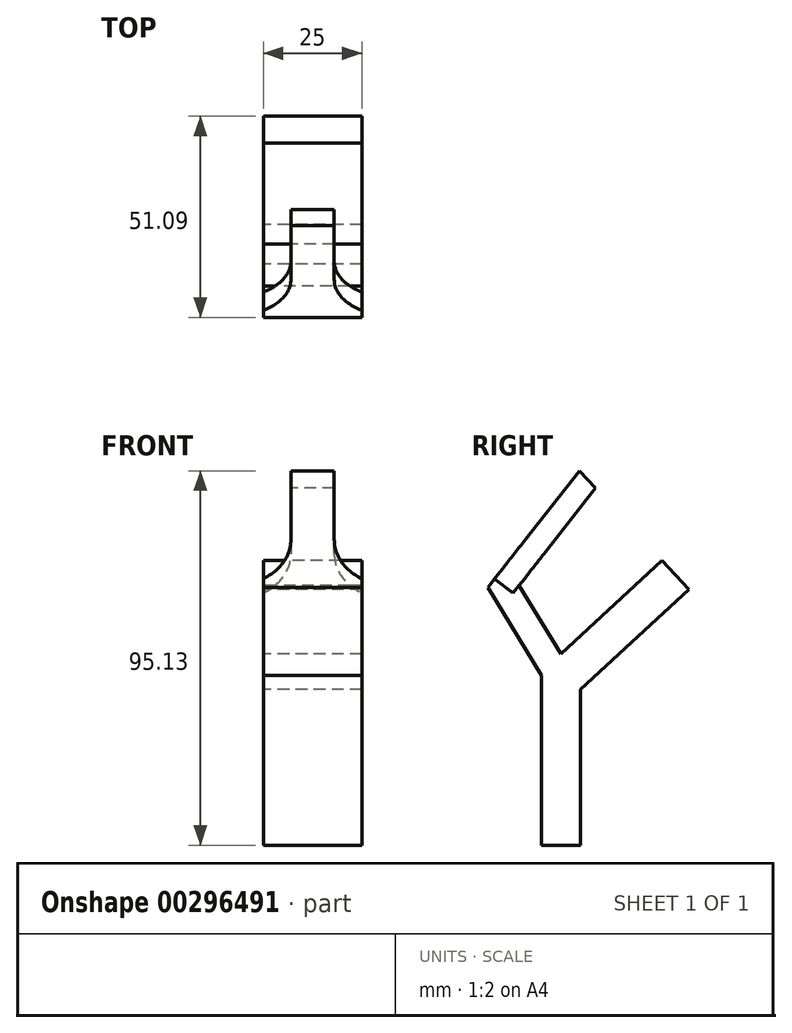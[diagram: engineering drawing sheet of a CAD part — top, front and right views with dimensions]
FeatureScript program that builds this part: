
annotation { "Feature Type Name" : "Feature", "Feature Type Description" : "" }
export const myFeature = defineFeature(function(context is Context, id is Id, definition is map)
    precondition{}
    {
        {
            var Q0;
            Q0=qCreatedBy(makeId("Right.planeOp"),FACE);
            var sketch = newSketch(context, id + "F0", { "sketchPlane" : qUnion([Q0])});
            skLineSegment(sketch, "E0", {"start": v(23.6, 39.62) * mm, "end": v(51.1, 65) * mm});
            skLineSegment(sketch, "E1", {"start": v(51.1, 65) * mm, "end": v(44.31, 72.35) * mm});
            skLineSegment(sketch, "E2", {"start": v(44.31, 72.35) * mm, "end": v(18.6, 48.6) * mm});
            skLineSegment(sketch, "E3", {"start": v(18.6, 48.6) * mm, "end": v(7.97, 66.02) * mm});
            skLineSegment(sketch, "E4", {"start": v(7.97, 66.02) * mm, "end": v(27.35, 90.72) * mm});
            skLineSegment(sketch, "E5", {"start": v(27.35, 90.72) * mm, "end": v(23.29, 95.13) * mm});
            skLineSegment(sketch, "E6", {"start": v(23.29, 95.13) * mm, "end": v(0, 65.46) * mm});
            skLineSegment(sketch, "E7", {"start": v(-34.13, 0) * mm, "end": v(0, 0) * mm});
            skLineSegment(sketch, "E8", {"start": v(51.1, 65) * mm, "end": v(27.45, 90.62) * mm, "construction": true});
            skLineSegment(sketch, "E9", {"start": v(18.6, 35) * mm, "end": v(18.6, 0) * mm, "construction": true});
            skLineSegment(sketch, "E10", {"start": v(13.6, 43.2) * mm, "end": v(13.6, 0) * mm});
            skLineSegment(sketch, "E11", {"start": v(13.6, 0) * mm, "end": v(23.6, 0) * mm});
            skLineSegment(sketch, "E12", {"start": v(23.6, 0) * mm, "end": v(23.6, 39.62) * mm});
            skLineSegment(sketch, "E13", {"start": v(0, 65.46) * mm, "end": v(13.6, 43.2) * mm});
            skSolve(sketch);
        }
        {
            var Q0;
            Q0=makeQuery(id+"F0.imprint","IMPRINT",FACE,{"disambiguationData":[TD([[makeQuery(id+"F0.imprint","IMPRINT",EDGE,{"derivedFrom":sQuery(id+"F0.wireOp",EDGE,"E0")}),1.0]])]});
            extrude(context, id + "F1", {"entities" : qUnion([Q0]), "endBound" : BoundingType.SYMMETRIC, "depth" : 25 * mm, "hasSecondDirection" : true, "secondDirectionOppositeDirection" : true, "secondDirectionDepth" : 25 * mm});
        }
        {
            var Q0;
            Q0=makeQuery(id+"F1.opExtrude","SWEPT_FACE",FACE,{"disambiguationData":[OSD([sQuery(id+"F0.wireOp",EDGE,"E6")])]});
            var sketch = newSketch(context, id + "F2", { "sketchPlane" : qUnion([Q0])});
            skLineSegment(sketch, "E14", {"start": v(-20.2, 52.04) * mm, "end": v(20.44, 52.04) * mm, "construction": true});
            skCircle(sketch, "E15", {"center": v(-20.5, 67.04) * mm, "radius": 15 * mm});
            skCircle(sketch, "E16", {"center": v(20.5, 67.04) * mm, "radius": 15 * mm});
            skLineSegment(sketch, "E17", {"start": v(-20.5, 67.04) * mm, "end": v(20.5, 67.04) * mm, "construction": true});
            skPoint(sketch, "E18", {"position": v(0, 67.04) * mm});
            skLineSegment(sketch, "E19", {"start": v(-5.5, 67.04) * mm, "end": v(-5.5, 89.2) * mm});
            skLineSegment(sketch, "E20", {"start": v(5.5, 67.04) * mm, "end": v(5.5, 89.2) * mm});
            skLineSegment(sketch, "E21", {"start": v(5.5, 89.2) * mm, "end": v(-5.5, 89.2) * mm});
            skSolve(sketch);
        }
        {
            var Q0;
            Q0=qSketchRegion(id+"F2",true);
            var Q1;
            {var subQ0=sQuery(id+"F2.wireOp",EDGE,"E19");Q1=makeQuery(id+"F2.imprint","IMPRINT",FACE,{"disambiguationData":[TD([[makeQuery(id+"F2.imprint","IMPRINT",EDGE,{"derivedFrom":subQ0}),1.0]])]});}
            var Q2;
            {var subQ0=sQuery(id+"F2.wireOp",EDGE,"E20");Q2=makeQuery(id+"F2.imprint","IMPRINT",FACE,{"disambiguationData":[TD([[makeQuery(id+"F2.imprint","IMPRINT",EDGE,{"derivedFrom":subQ0}),-1.0]])]});}
            var Q3;
            Q3=makeQuery(id+"F1.opExtrude","SWEPT_FACE",FACE,{"disambiguationData":[OSD([sQuery(id+"F0.wireOp",EDGE,"E4")])]});
            extrude(context, id + "F3", {"entities" : qUnion([Q0, Q1, Q2]), "operationType" : NewBodyOperationType.REMOVE, "endBound" : BoundingType.UP_TO_SURFACE, "oppositeDirection" : true, "endBoundEntityFace" : qUnion([Q3]), "depth" : 25 * mm});
        }
    });
